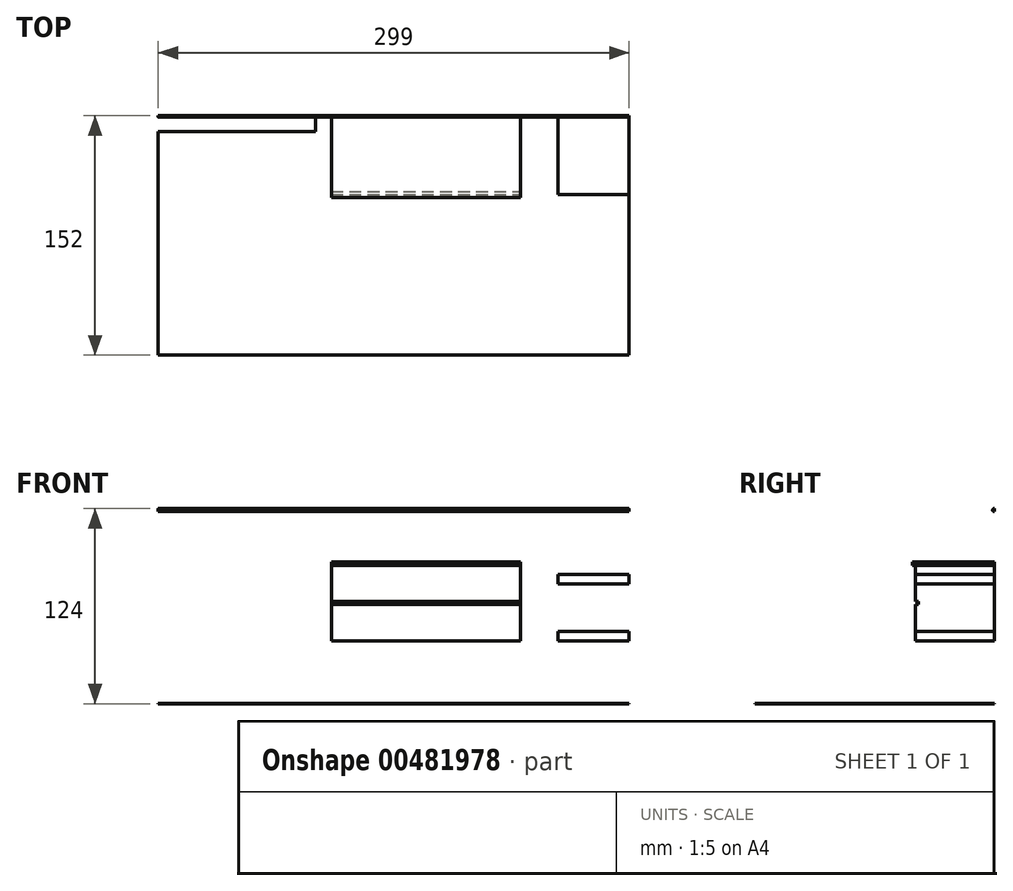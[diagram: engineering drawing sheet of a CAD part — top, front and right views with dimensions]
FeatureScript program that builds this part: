
annotation { "Feature Type Name" : "Feature", "Feature Type Description" : "" }
export const myFeature = defineFeature(function(context is Context, id is Id, definition is map)
    precondition{}
    {
        {
            var Q0;
            Q0=qCreatedBy(makeId("Top.planeOp"),FACE);
            var sketch = newSketch(context, id + "F0", { "sketchPlane" : qUnion([Q0])});
            skLineSegment(sketch, "E0", {"start": v(0, 0) * mm, "end": v(0, -52) * mm});
            skLineSegment(sketch, "E1", {"start": v(0, 0) * mm, "end": v(-199, 0) * mm});
            skLineSegment(sketch, "E2", {"start": v(-199, 0) * mm, "end": v(-199, -10) * mm});
            skLineSegment(sketch, "E3", {"start": v(-199, -10) * mm, "end": v(-299, -10) * mm});
            skLineSegment(sketch, "E4", {"start": v(-299, -10) * mm, "end": v(-299, -152) * mm});
            skLineSegment(sketch, "E5", {"start": v(-299, -152) * mm, "end": v(0, -152) * mm});
            skLineSegment(sketch, "E6", {"start": v(0, -52) * mm, "end": v(0, -152) * mm});
            skSolve(sketch);
        }
        {
            var Q0;
            Q0=sQuery(id+"F0.wireOp",EDGE,"E3");
            var Q1;
            Q1=sQuery(id+"F0.wireOp",EDGE,"E2");
            var Q2;
            Q2=sQuery(id+"F0.wireOp",EDGE,"E1");
            var Q3;
            Q3=sQuery(id+"F0.wireOp",EDGE,"E0");
            extrude(context, id + "F1", {"bodyType" : ToolBodyType.SURFACE, "surfaceEntities" : qUnion([Q0, Q1, Q2, Q3]), "depth" : 122 * mm});
        }
        {
            var Q0;
            Q0=makeQuery(id+"F0.imprint","IMPRINT",FACE,{"disambiguationData":[TD([[makeQuery(id+"F0.imprint","IMPRINT",EDGE,{"derivedFrom":sQuery(id+"F0.wireOp",EDGE,"E0")}),-1.0]])]});
            extrude(context, id + "F2", {"entities" : qUnion([Q0]), "depth" : 0.1 * mm});
        }
        {
            var Q0;
            Q0=makeQuery(id+"F1.opExtrude","SWEPT_FACE",FACE,{"disambiguationData":[OSD([sQuery(id+"F0.wireOp",EDGE,"E1")])]});
            var sketch = newSketch(context, id + "F3", { "sketchPlane" : qUnion([Q0])});
            skLineSegment(sketch, "E7.bottom", {"start": v(189, 88) * mm, "end": v(69, 88) * mm});
            skLineSegment(sketch, "E7.top", {"start": v(189, 40) * mm, "end": v(69, 40) * mm});
            skLineSegment(sketch, "E7.left", {"start": v(189, 88) * mm, "end": v(189, 40) * mm});
            skLineSegment(sketch, "E7.right", {"start": v(69, 88) * mm, "end": v(69, 40) * mm});
            skLineSegment(sketch, "E8.top", {"start": v(189, 90) * mm, "end": v(69, 90) * mm});
            skLineSegment(sketch, "E8.left", {"start": v(189, 88) * mm, "end": v(189, 90) * mm});
            skLineSegment(sketch, "E8.right", {"start": v(69, 88) * mm, "end": v(69, 90) * mm});
            skLineSegment(sketch, "E9.bottom", {"start": v(189, 65) * mm, "end": v(69, 65) * mm});
            skLineSegment(sketch, "E9.top", {"start": v(189, 63) * mm, "end": v(69, 63) * mm});
            skLineSegment(sketch, "E9.left", {"start": v(189, 65) * mm, "end": v(189, 63) * mm});
            skLineSegment(sketch, "E9.right", {"start": v(69, 65) * mm, "end": v(69, 63) * mm});
            skLineSegment(sketch, "E10.bottom", {"start": v(0, 40) * mm, "end": v(45, 40) * mm});
            skLineSegment(sketch, "E10.top", {"start": v(0, 46) * mm, "end": v(45, 46) * mm});
            skLineSegment(sketch, "E10.left", {"start": v(0, 40) * mm, "end": v(0, 46) * mm});
            skLineSegment(sketch, "E10.right", {"start": v(45, 40) * mm, "end": v(45, 46) * mm});
            skLineSegment(sketch, "E11.bottom", {"start": v(0, 76) * mm, "end": v(45, 76) * mm});
            skLineSegment(sketch, "E11.top", {"start": v(0, 82) * mm, "end": v(45, 82) * mm});
            skLineSegment(sketch, "E11.left", {"start": v(0, 76) * mm, "end": v(0, 82) * mm});
            skLineSegment(sketch, "E11.right", {"start": v(45, 76) * mm, "end": v(45, 82) * mm});
            skLineSegment(sketch, "E12.bottom", {"start": v(0, 116) * mm, "end": v(30, 116) * mm});
            skLineSegment(sketch, "E12.top", {"start": v(0, 122) * mm, "end": v(30, 122) * mm});
            skLineSegment(sketch, "E12.left", {"start": v(0, 116) * mm, "end": v(0, 122) * mm});
            skLineSegment(sketch, "E12.right", {"start": v(30, 116) * mm, "end": v(30, 122) * mm});
            skSolve(sketch);
        }
        {
            var Q0;
            Q0=makeQuery(id+"F3.imprint","IMPRINT",FACE,{"disambiguationData":[TD([[makeQuery(id+"F3.imprint","IMPRINT",EDGE,{"derivedFrom":sQuery(id+"F3.wireOp",EDGE,"E9.bottom")}),1.0]])]});
            extrude(context, id + "F4", {"entities" : qUnion([Q0]), "oppositeDirection" : true, "depth" : 48 * mm});
        }
        {
            var Q0;
            {var subQ0=sQuery(id+"F3.wireOp",EDGE,"E7.bottom");Q0=makeQuery(id+"F3.imprint","IMPRINT",FACE,{"disambiguationData":[TD([[makeQuery(id+"F3.imprint","IMPRINT",EDGE,{"derivedFrom":subQ0}),1.0]])]});}
            var Q1;
            {var subQ0=sQuery(id+"F3.wireOp",EDGE,"E7.top");Q1=makeQuery(id+"F3.imprint","IMPRINT",FACE,{"disambiguationData":[TD([[makeQuery(id+"F3.imprint","IMPRINT",EDGE,{"derivedFrom":subQ0}),-1.0]])]});}
            extrude(context, id + "F5", {"entities" : qUnion([Q0, Q1]), "operationType" : NewBodyOperationType.ADD, "oppositeDirection" : true, "depth" : 50 * mm});
        }
        {
            var Q0;
            Q0=makeQuery(id+"F3.imprint","IMPRINT",FACE,{"disambiguationData":[TD([[makeQuery(id+"F3.imprint","IMPRINT",EDGE,{"derivedFrom":sQuery(id+"F3.wireOp",EDGE,"E7.bottom")}),-1.0]])]});
            extrude(context, id + "F6", {"entities" : qUnion([Q0]), "oppositeDirection" : true, "depth" : 52 * mm});
        }
        {
            var Q0;
            Q0=makeQuery(id+"F1.opExtrude","SWEPT_FACE",FACE,{"disambiguationData":[OSD([sQuery(id+"F0.wireOp",EDGE,"E0")])]});
            var sketch = newSketch(context, id + "F7", { "sketchPlane" : qUnion([Q0])});
            skLineSegment(sketch, "E13", {"start": v(0, 122) * mm, "end": v(0, 124) * mm});
            skArc(sketch, "E14", {"start": v(0, 124) * mm, "mid": v(-1, 123) * mm, "end": v(0, 122) * mm});
            skLineSegment(sketch, "E15.0", {"start": v(-10, 122) * mm, "end": v(0, 122) * mm});
            skSolve(sketch);
        }
        {
            var Q0;
            Q0=makeQuery(id+"F7.imprint","IMPRINT",FACE,{"disambiguationData":[TD([[makeQuery(id+"F7.imprint","IMPRINT",EDGE,{"derivedFrom":sQuery(id+"F7.wireOp",EDGE,"E13")}),1.0]])]});
            extrude(context, id + "F8", {"entities" : qUnion([Q0]), "oppositeDirection" : true, "depth" : 299 * mm});
        }
        {
            var Q0;
            Q0=sQuery(id+"F7.wireOp",EDGE,"E15.0");
            var Q1;
            Q1=makeQuery(id+"F1.opExtrude","SWEPT_FACE",FACE,{"disambiguationData":[OSD([sQuery(id+"F0.wireOp",EDGE,"E2")])]});
            extrude(context, id + "F9", {"bodyType" : ToolBodyType.SURFACE, "surfaceEntities" : qUnion([Q0]), "oppositeDirection" : true, "depth" : 299 * mm, "hasSecondDirection" : true, "secondDirectionBound" : SecondDirectionBoundingType.UP_TO_SURFACE, "secondDirectionOppositeDirection" : true, "secondDirectionBoundEntityFace" : qUnion([Q1]), "secondDirectionDepth" : 25 * mm});
        }
        {
            var Q0;
            Q0=makeQuery(id+"F3.imprint","IMPRINT",FACE,{"disambiguationData":[TD([[makeQuery(id+"F3.imprint","IMPRINT",EDGE,{"derivedFrom":sQuery(id+"F3.wireOp",EDGE,"E11.bottom")}),1.0]])]});
            var Q1;
            Q1=makeQuery(id+"F3.imprint","IMPRINT",FACE,{"disambiguationData":[TD([[makeQuery(id+"F3.imprint","IMPRINT",EDGE,{"derivedFrom":sQuery(id+"F3.wireOp",EDGE,"E10.bottom")}),1.0]])]});
            extrude(context, id + "F10", {"entities" : qUnion([Q0, Q1]), "oppositeDirection" : true, "depth" : 50 * mm});
        }
    });
